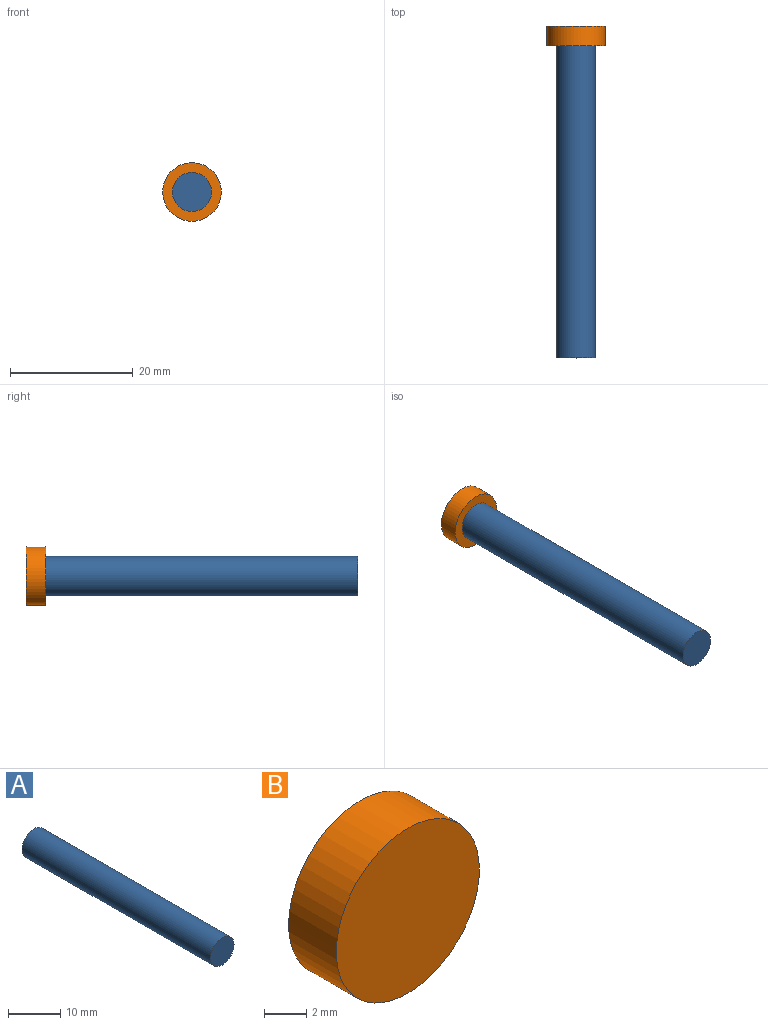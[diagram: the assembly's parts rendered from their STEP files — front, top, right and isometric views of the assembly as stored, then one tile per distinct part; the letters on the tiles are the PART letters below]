
ASSEMBLY  parts=2 mates=1
PART A: 3 faces, bbox 6.4x50.8x6.4 mm
  f0: cylinder r=3.17mm len=50.8mm, axis (0,1,0), area 1013.4mm2, adj f1,f2
  f1: plane 6.35x6.35mm, normal (0,-1,0), area 31.7mm2, adj f0
  f2: plane 6.35x6.35mm, normal (0,1,0), area 31.7mm2, adj f0
PART B: 3 faces, bbox 9.5x3.2x9.5 mm
  f0: cylinder r=4.76mm len=9.53mm, axis (0,1,0), area 95mm2, adj f1,f2
  f1: plane 9.53x9.53mm, normal (0,-1,0), area 71.3mm2, adj f0
  f2: plane 9.53x9.53mm, normal (0,1,0), area 71.3mm2, adj f0
PLACE A t=(-1.89,-4.01,-4.38)mm
PLACE B t=(26.61,-0.84,24.97)mm
MATE fastened B.f0 <-> A.f0  axis (0,-1,0) through (-19.88,-4.01,11.59)mm
